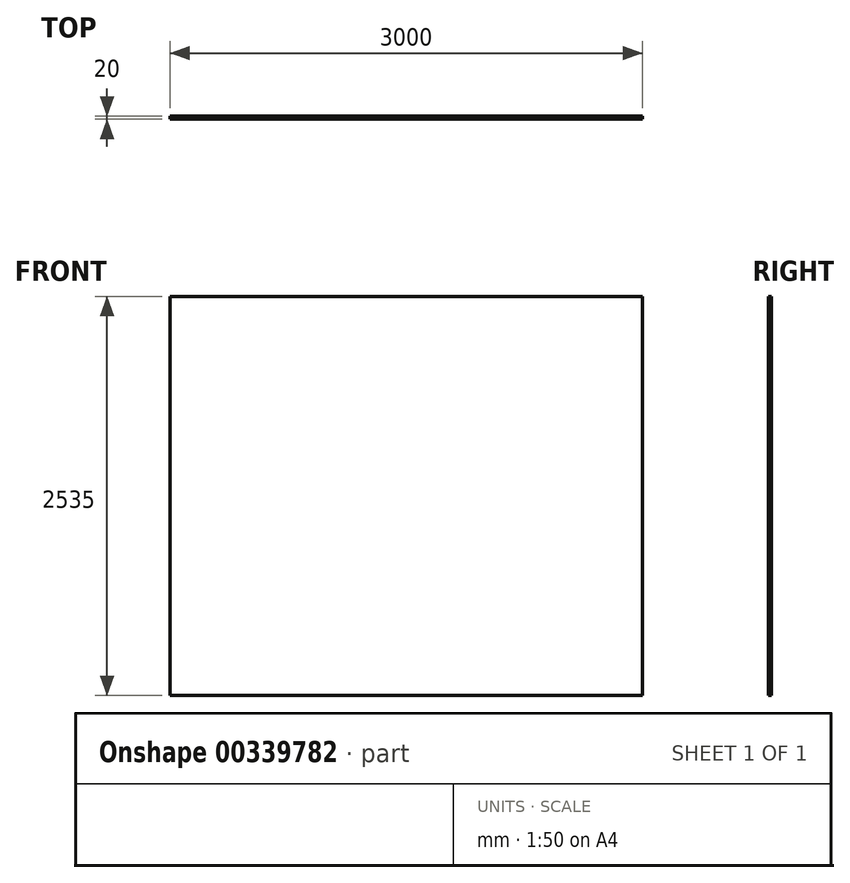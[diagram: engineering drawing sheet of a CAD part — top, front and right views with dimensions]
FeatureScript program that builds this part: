
annotation { "Feature Type Name" : "Feature", "Feature Type Description" : "" }
export const myFeature = defineFeature(function(context is Context, id is Id, definition is map)
    precondition{}
    {
        {
            var Q0;
            Q0=qCreatedBy(makeId("Front.planeOp"),FACE);
            var sketch = newSketch(context, id + "F0", { "sketchPlane" : qUnion([Q0])});
            skLineSegment(sketch, "E0.bottom", {"start": v(0, 0) * mm, "end": v(3000, 0) * mm});
            skLineSegment(sketch, "E0.top", {"start": v(0, 2535) * mm, "end": v(3000, 2535) * mm});
            skLineSegment(sketch, "E0.left", {"start": v(0, 0) * mm, "end": v(0, 2535) * mm});
            skLineSegment(sketch, "E0.right", {"start": v(3000, 0) * mm, "end": v(3000, 2535) * mm});
            skSolve(sketch);
        }
        {
            var Q0;
            Q0=makeQuery(id+"F0.imprint","IMPRINT",FACE,{"disambiguationData":[TD([[makeQuery(id+"F0.imprint","IMPRINT",EDGE,{"derivedFrom":sQuery(id+"F0.wireOp",EDGE,"E0.bottom")}),1.0]])]});
            extrude(context, id + "F1", {"entities" : qUnion([Q0]), "depth" : 20 * mm});
        }
    });
